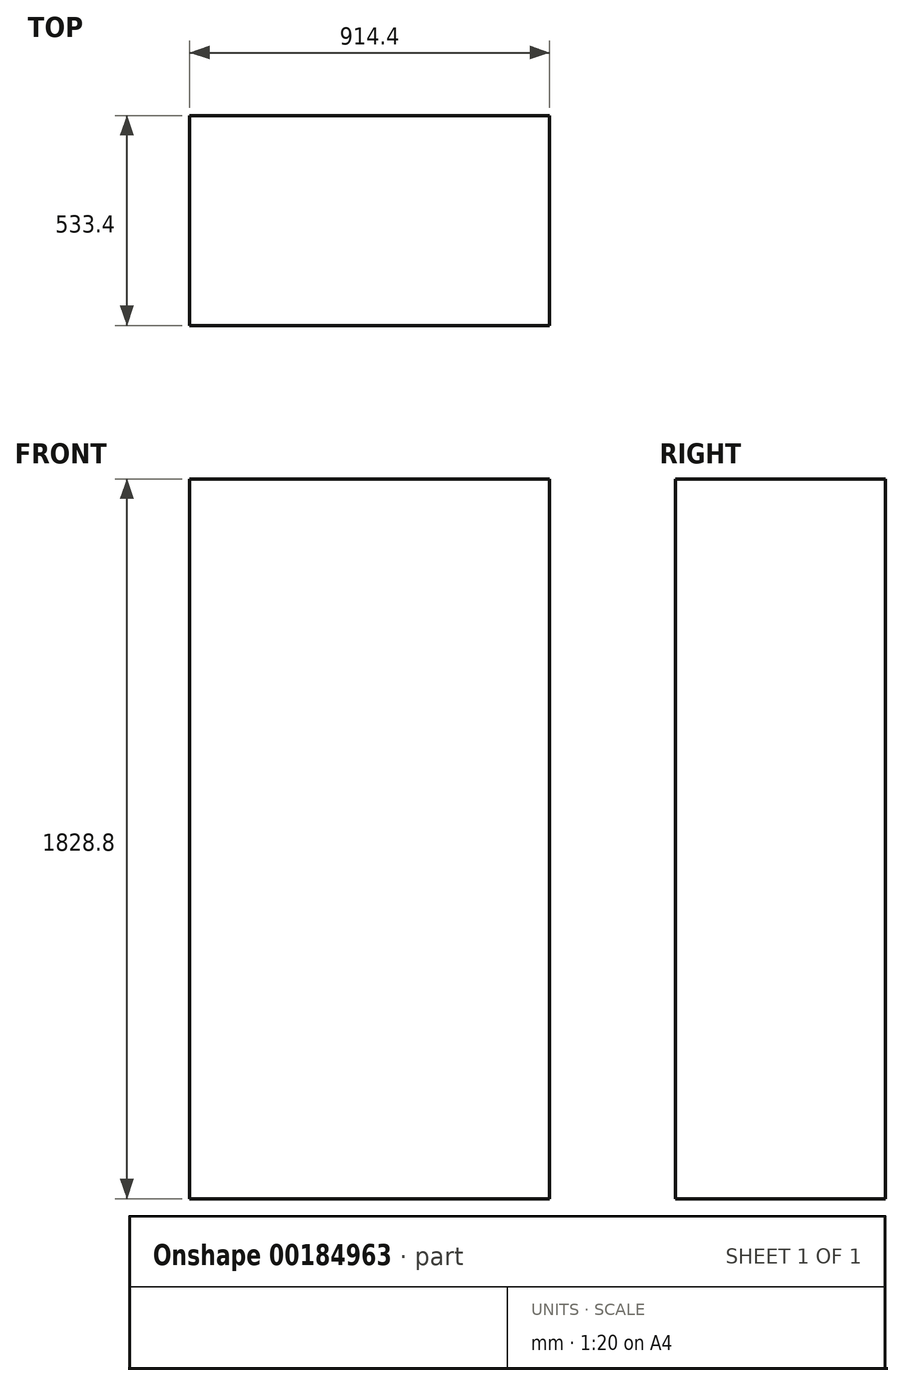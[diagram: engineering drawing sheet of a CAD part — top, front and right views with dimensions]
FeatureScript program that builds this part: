
annotation { "Feature Type Name" : "Feature", "Feature Type Description" : "" }
export const myFeature = defineFeature(function(context is Context, id is Id, definition is map)
    precondition{}
    {
        {
            var Q0;
            Q0=qCreatedBy(makeId("Top.planeOp"),FACE);
            var sketch = newSketch(context, id + "F0", { "sketchPlane" : qUnion([Q0])});
            skLineSegment(sketch, "E0.bottom", {"start": v(457.2, 266.7) * mm, "end": v(-457.2, 266.7) * mm});
            skLineSegment(sketch, "E0.top", {"start": v(457.2, -266.7) * mm, "end": v(-457.2, -266.7) * mm});
            skLineSegment(sketch, "E0.left", {"start": v(457.2, 266.7) * mm, "end": v(457.2, -266.7) * mm});
            skLineSegment(sketch, "E0.right", {"start": v(-457.2, 266.7) * mm, "end": v(-457.2, -266.7) * mm});
            skPoint(sketch, "E0.middle", {"position": v(0, 0) * mm});
            skSolve(sketch);
        }
        {
            var Q0;
            Q0=makeQuery(id+"F0.imprint","IMPRINT",FACE,{"disambiguationData":[TD([[makeQuery(id+"F0.imprint","IMPRINT",EDGE,{"derivedFrom":sQuery(id+"F0.wireOp",EDGE,"E0.bottom")}),1.0]])]});
            extrude(context, id + "F1", {"entities" : qUnion([Q0]), "depth" : 1828.8 * mm});
        }
    });
